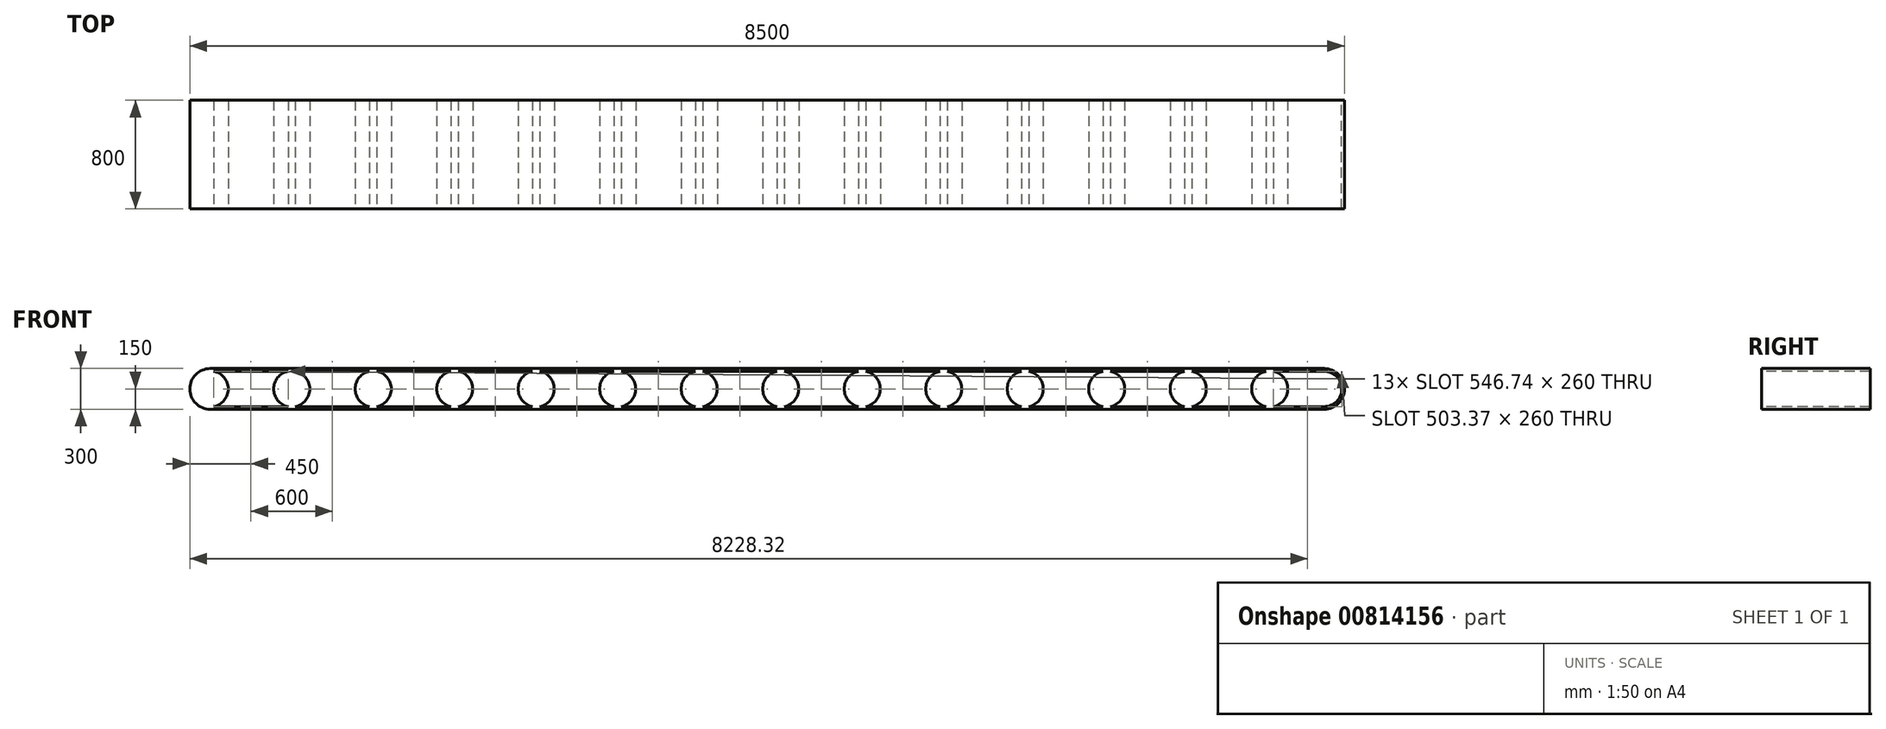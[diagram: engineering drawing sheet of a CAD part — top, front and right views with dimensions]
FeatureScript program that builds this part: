
annotation { "Feature Type Name" : "Feature", "Feature Type Description" : "" }
export const myFeature = defineFeature(function(context is Context, id is Id, definition is map)
    precondition{}
    {
        {
            var Q0;
            Q0=qCreatedBy(makeId("Front.planeOp"),FACE);
            var sketch = newSketch(context, id + "F0", { "sketchPlane" : qUnion([Q0])});
            skLineSegment(sketch, "E0.bottom", {"start": v(150, 0) * mm, "end": v(8350, 0) * mm});
            skLineSegment(sketch, "E0.top", {"start": v(150, 300) * mm, "end": v(8350, 300) * mm});
            skLineSegment(sketch, "E0.left", {"start": v(0, 150) * mm, "end": v(0, 150) * mm});
            skLineSegment(sketch, "E0.right", {"start": v(8500, 150) * mm, "end": v(8500, 150) * mm});
            skPoint(sketch, "E1.visualSharp", {"position": v(0, 300) * mm});
            skArc(sketch, "E1.filletArc", {"start": v(150, 300) * mm, "mid": v(43.93, 256.07) * mm, "end": v(0, 150) * mm});
            skPoint(sketch, "E2.visualSharp", {"position": v(0, 0) * mm});
            skArc(sketch, "E2.filletArc", {"start": v(0, 150) * mm, "mid": v(43.93, 43.93) * mm, "end": v(150, 0) * mm});
            skPoint(sketch, "E3.visualSharp", {"position": v(8500, 300) * mm});
            skArc(sketch, "E3.filletArc", {"start": v(8500, 150) * mm, "mid": v(8456.07, 256.07) * mm, "end": v(8350, 300) * mm});
            skPoint(sketch, "E4.visualSharp", {"position": v(8500, 0) * mm});
            skArc(sketch, "E4.filletArc", {"start": v(8350, 0) * mm, "mid": v(8456.07, 43.93) * mm, "end": v(8500, 150) * mm});
            skSolve(sketch);
        }
        {
            var Q0;
            Q0=makeQuery(id+"F0.imprint","IMPRINT",FACE,{"disambiguationData":[TD([[makeQuery(id+"F0.imprint","IMPRINT",EDGE,{"derivedFrom":sQuery(id+"F0.wireOp",EDGE,"E0.bottom")}),1.0]])]});
            extrude(context, id + "F1", {"entities" : qUnion([Q0]), "depth" : 800 * mm, "offsetDistance" : 25 * mm});
        }
        {
            var Q0;
            Q0=makeQuery(id+"F1.opExtrude","CAP_FACE",FACE,{"disambiguationData":[OSD([sQuery(id+"F0.wireOp",EDGE,"E0.bottom"),sQuery(id+"F0.wireOp",EDGE,"E0.top"),sQuery(id+"F0.wireOp",EDGE,"E1.filletArc"),sQuery(id+"F0.wireOp",EDGE,"E2.filletArc"),sQuery(id+"F0.wireOp",EDGE,"E3.filletArc"),sQuery(id+"F0.wireOp",EDGE,"E4.filletArc")])],"isStart":false});
            shell(context, id + "F2", {"entities" : qUnion([Q0]), "thickness" : 20 * mm});
        }
        {
            var Q0;
            Q0=makeQuery(id+"F2.opShell","OFFSET_FACE",FACE,{"disambiguationData":[OSD([sQuery(id+"F0.wireOp",EDGE,"E0.bottom"),sQuery(id+"F0.wireOp",EDGE,"E0.top"),sQuery(id+"F0.wireOp",EDGE,"E1.filletArc"),sQuery(id+"F0.wireOp",EDGE,"E2.filletArc"),sQuery(id+"F0.wireOp",EDGE,"E3.filletArc"),sQuery(id+"F0.wireOp",EDGE,"E4.filletArc")])]});
            extrude(context, id + "F3", {"entities" : qUnion([Q0]), "operationType" : NewBodyOperationType.REMOVE, "oppositeDirection" : true, "depth" : 25 * mm, "offsetDistance" : 25 * mm});
        }
        {
            var Q0;
            Q0=makeQuery(id+"F1.opExtrude","CAP_FACE",FACE,{"disambiguationData":[OSD([sQuery(id+"F0.wireOp",EDGE,"E0.bottom"),sQuery(id+"F0.wireOp",EDGE,"E0.top"),sQuery(id+"F0.wireOp",EDGE,"E1.filletArc"),sQuery(id+"F0.wireOp",EDGE,"E2.filletArc"),sQuery(id+"F0.wireOp",EDGE,"E3.filletArc"),sQuery(id+"F0.wireOp",EDGE,"E4.filletArc")])],"isStart":false});
            var sketch = newSketch(context, id + "F4", { "sketchPlane" : qUnion([Q0])});
            skCircle(sketch, "E5", {"center": v(150, 150) * mm, "radius": 132.7 * mm});
            skCircle(sketch, "E6.1.0.0", {"center": v(750, 150) * mm, "radius": 132.7 * mm});
            skCircle(sketch, "E6.2.0.0", {"center": v(1350, 150) * mm, "radius": 132.7 * mm});
            skCircle(sketch, "E6.3.0.0", {"center": v(1950, 150) * mm, "radius": 132.7 * mm});
            skCircle(sketch, "E6.4.0.0", {"center": v(2550, 150) * mm, "radius": 132.7 * mm});
            skCircle(sketch, "E6.5.0.0", {"center": v(3150, 150) * mm, "radius": 132.7 * mm});
            skCircle(sketch, "E6.6.0.0", {"center": v(3750, 150) * mm, "radius": 132.7 * mm});
            skCircle(sketch, "E6.7.0.0", {"center": v(4350, 150) * mm, "radius": 132.7 * mm});
            skCircle(sketch, "E6.8.0.0", {"center": v(4950, 150) * mm, "radius": 132.7 * mm});
            skCircle(sketch, "E6.9.0.0", {"center": v(5550, 150) * mm, "radius": 132.7 * mm});
            skCircle(sketch, "E6.10.0.0", {"center": v(6150, 150) * mm, "radius": 132.7 * mm});
            skCircle(sketch, "E6.11.0.0", {"center": v(6750, 150) * mm, "radius": 132.7 * mm});
            skCircle(sketch, "E6.12.0.0", {"center": v(7350, 150) * mm, "radius": 132.7 * mm});
            skCircle(sketch, "E6.13.0.0", {"center": v(7950, 150) * mm, "radius": 132.7 * mm});
            skLineSegment(sketch, "E6.direction1", {"start": v(150, 150) * mm, "end": v(750, 150) * mm, "construction": true});
            skSolve(sketch);
        }
        {
            var Q0;
            Q0 = qSketchRegion(id + "F4", true);
            extrude(context, id + "F5", {"entities" : qUnion([Q0]), "operationType" : NewBodyOperationType.ADD, "oppositeDirection" : true, "depth" : 800 * mm, "offsetDistance" : 25 * mm});
        }
    });
